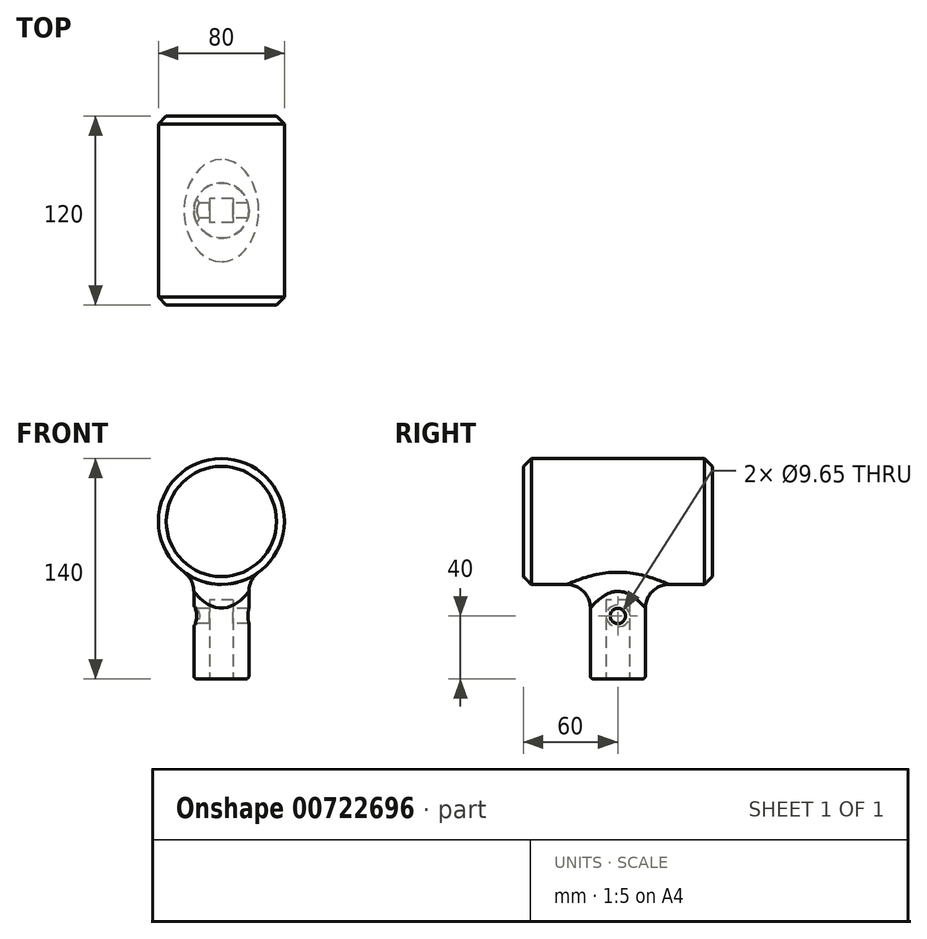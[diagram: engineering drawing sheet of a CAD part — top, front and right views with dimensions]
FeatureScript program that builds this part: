
annotation { "Feature Type Name" : "Feature", "Feature Type Description" : "" }
export const myFeature = defineFeature(function(context is Context, id is Id, definition is map)
    precondition{}
    {
        {
            var Q0;
            Q0=qCreatedBy(makeId("Front.planeOp"),FACE);
            var sketch = newSketch(context, id + "F0", { "sketchPlane" : qUnion([Q0])});
            skCircle(sketch, "E0", {"center": v(0, 0) * mm, "radius": 40 * mm});
            skSolve(sketch);
        }
        {
            var Q0;
            Q0 = qSketchRegion(id + "F0", true);
            extrude(context, id + "F1", {"entities" : qUnion([Q0]), "endBound" : BoundingType.SYMMETRIC, "depth" : 120 * mm, "offsetDistance" : 25 * mm});
        }
        {
            var Q0;
            Q0=qCreatedBy(makeId("Top.planeOp"),FACE);
            var sketch = newSketch(context, id + "F2", { "sketchPlane" : qUnion([Q0])});
            skCircle(sketch, "E1", {"center": v(0, 0) * mm, "radius": 17.5 * mm});
            skSolve(sketch);
        }
        {
            var Q0;
            Q0 = qSketchRegion(id + "F2", true);
            extrude(context, id + "F3", {"entities" : qUnion([Q0]), "operationType" : NewBodyOperationType.ADD, "oppositeDirection" : true, "depth" : 100 * mm, "offsetDistance" : 25 * mm});
        }
        {
            var Q0;
            Q0=makeQuery(id+"F3.opExtrude","CAP_FACE",FACE,{"disambiguationData":[OSD([sQuery(id+"F2.wireOp",EDGE,"E1")])],"isStart":false});
            var sketch = newSketch(context, id + "F4", { "sketchPlane" : qUnion([Q0])});
            skLineSegment(sketch, "E2.bottom", {"start": v(7.5, -7.5) * mm, "end": v(-7.5, -7.5) * mm});
            skLineSegment(sketch, "E2.top", {"start": v(7.5, 7.5) * mm, "end": v(-7.5, 7.5) * mm});
            skLineSegment(sketch, "E2.left", {"start": v(7.5, -7.5) * mm, "end": v(7.5, 7.5) * mm});
            skLineSegment(sketch, "E2.right", {"start": v(-7.5, -7.5) * mm, "end": v(-7.5, 7.5) * mm});
            skPoint(sketch, "E2.middle", {"position": v(0, 0) * mm});
            skSolve(sketch);
        }
        {
            var Q0;
            Q0 = qSketchRegion(id + "F4", true);
            extrude(context, id + "F5", {"entities" : qUnion([Q0]), "operationType" : NewBodyOperationType.REMOVE, "oppositeDirection" : true, "depth" : 50 * mm, "offsetDistance" : 25 * mm});
        }
        {
            var Q0;
            Q0=qCreatedBy(makeId("Right.planeOp"),FACE);
            var sketch = newSketch(context, id + "F6", { "sketchPlane" : qUnion([Q0])});
            skCircle(sketch, "E3", {"center": v(0, -60) * mm, "radius": 4.83 * mm});
            skSolve(sketch);
        }
        {
            var Q0;
            Q0 = qSketchRegion(id + "F6", true);
            extrude(context, id + "F7", {"entities" : qUnion([Q0]), "operationType" : NewBodyOperationType.REMOVE, "endBound" : BoundingType.SYMMETRIC, "depth" : 50 * mm, "offsetDistance" : 25 * mm});
        }
        {
            var Q0;
            Q0=makeQuery(id+"F1.opExtrude","CAP_EDGE",EDGE,{"disambiguationData":[OSD([sQuery(id+"F0.wireOp",EDGE,"E0")])],"isStart":true});
            var Q1;
            Q1=makeQuery(id+"F1.opExtrude","CAP_EDGE",EDGE,{"disambiguationData":[OSD([sQuery(id+"F0.wireOp",EDGE,"E0")])],"isStart":false});
            chamfer(context, id + "F8", {"entities" : qUnion([Q0, Q1]), "width" : 5 * mm, "tangentPropagation" : true});
        }
        {
            var Q0;
            Q0=makeQuery(id+"F3.boolean.opBoolean","INTERSECT",EDGE,{"derivedFrom":[makeQuery(id+"F1.opExtrude","SWEPT_FACE",FACE,{"disambiguationData":[OSD([sQuery(id+"F0.wireOp",EDGE,"E0")])]}),makeQuery(id+"F3.opExtrude","SWEPT_FACE",FACE,{"disambiguationData":[OSD([sQuery(id+"F2.wireOp",EDGE,"E1")])]})]});
            fillet(context, id + "F9", {"entities" : qUnion([Q0]), "radius" : 15 * mm, "tangentPropagation" : true, "allowEdgeOverflow" : false});
        }
        {
            var Q0;
            Q0=makeQuery(id+"F3.opExtrude","CAP_EDGE",EDGE,{"disambiguationData":[OSD([sQuery(id+"F2.wireOp",EDGE,"E1")])],"isStart":false});
            fillet(context, id + "F10", {"entities" : qUnion([Q0]), "radius" : 2 * mm, "tangentPropagation" : true, "allowEdgeOverflow" : false});
        }
        {
            var Q0;
            Q0=makeQuery(id+"F7.boolean.opBoolean","INTERSECT",EDGE,{"disambiguationData":[OD(1.0)],"derivedFrom":[makeQuery(id+"F3.opExtrude","SWEPT_FACE",FACE,{"disambiguationData":[OSD([sQuery(id+"F2.wireOp",EDGE,"E1")])]}),makeQuery(id+"F7.opExtrude","SWEPT_FACE",FACE,{"disambiguationData":[OSD([sQuery(id+"F6.wireOp",EDGE,"E3")])]})]});
            chamfer(context, id + "F11", {"entities" : qUnion([Q0]), "width" : 2 * mm, "tangentPropagation" : true});
        }
    });
